# Revit family: Serene_T&T_Window_E_Custom
name_source: partatom
category: Windows
revit_build: Autodesk Revit 2014 (Build: 20130308_1515(x64)
units: mm (PartAtom-declared; Revit-internal decimal feet)

## types (1)
- Serene_T&T_Window_E_Custom
    Area Glazing Fixed Panel Left = 0.13 m²
    Area Glazing Fixed Panel Right = 0.35 m²
    Area Glazing Sash = 0.43 m²
    Centered In Wall = Yes
    Custom SHGC Value = 0
    Custom Sash Height = 1122 mm
    Custom Sash Width = 522 mm  [stored 1.7126 ft]
    Custom U Value = 0
    Custom Windload = 1000 mm  [stored 3.28084 ft]
    Custom Window Exterior Offset = 0 mm  [stored 0 ft]
    Custom Window Height = 1490 mm  [stored 4.88845 ft]
    Custom Window Width = 890 mm  [stored 2.91995 ft]
    DG Gasket Finish = Double Glazing Gasket Material
    DG Gasket Tickness = 12 mm  [stored 0.0393701 ft]
    DG Thickness Calc = 4 mm  [stored 0.0131234 ft]
    Default Sill Height = 800 mm  [stored 2.62467 ft]
    Description = Tilt and turn window, Type E custom
    Fixed Panel Left Height = 260 mm
    Fixed Panel Left Width = 510 mm
    Fixed Panel Right Height = 1410 mm  [stored 4.62598 ft]
    Fixed Panel Right Width = 260 mm
    Frame Thickness = 52 mm
    Frame Width = 62 mm  [stored 0.203412 ft]
    Heavy Duty Mullion = No
    Height = 1490 mm  [stored 4.88845 ft]
    Length Decorative Mullion = 1490 mm  [stored 4.88845 ft]
    Length Mullion = 1410 mm  [stored 4.62598 ft]
    Length Transom = 510 mm
    Limit Fixed Panel Height Max = 1800 mm  [stored 5.90551 ft]
    Limit Fixed Panel Height Min = 200 mm  [stored 0.656168 ft]
    Limit Fixed Panel Width Max = 1800 mm  [stored 5.90551 ft]
    Limit Fixed Panel Width Min = 200 mm  [stored 0.656168 ft]
    Limit Sash Height Max = 1500 mm  [stored 4.92126 ft]
    Limit Sash Height Min = 300 mm  [stored 0.984252 ft]
    Limit Sash Width Max = 700 mm  [stored 2.29659 ft]
    Limit Sash Width Min = 300 mm  [stored 0.984252 ft]
    Limit Window Height Max = 1880 mm  [stored 6.16798 ft]
    Limit Window Height Min = 1430 mm
    Limit Window Width Max = 2430 mm
    Limit Window Width Min = 830 mm  [stored 2.7231 ft]
    Manufacturer = Crealco
    Max Pane Area = 0.43 m²
    Max System DG One Piece Thickness = 4 mm  [stored 0.0131234 ft]
    Max System DG Unit Thickness = 20 mm  [stored 0.0656168 ft]
    Model = Serene
    Sash Edge Gap = 34 mm
    Sash Frame Gasket = 3 mm  [stored 0.00984252 ft]
    Sash Height = 1122 mm
    Sash Overlap = 28 mm  [stored 0.0918635 ft]
    Sash Width = 522 mm  [stored 1.7126 ft]
    Standard Mullion = Yes
    URL = http://www.crealco.co.za
    Wall Closure = By host
    Width = 890 mm  [stored 2.91995 ft]
    Windload Design = 1000 mm  [stored 3.28084 ft]

note: [stored X ft] marks values corroborated as IEEE doubles in the binary element streams (Revit-internal decimal feet)

## geometry (parser evidence)
native form markers: Sweep x43
no freeform markers — native parametric forms only
